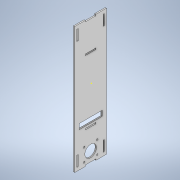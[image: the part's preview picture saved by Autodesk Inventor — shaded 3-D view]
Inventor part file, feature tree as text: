
AUTODESK INVENTOR PART (.ipt)
format: ipt  version: 2020 (Build 240168000, 168)  size: 261,120 bytes
history: native  units: in
note: dims shown in document units (in); Inventor stores cm internally (conversion verified against a paired STEP export)
features: sketch x12, extrude x11
ambient origin geometry x8: Origin, YZ Plane, XZ Plane, XY Plane, X Axis, Y Axis, Z Axis, Center Point
bodies: Solid1 (feature_tree)
feature tree (23):
  extrude  "Extrusion1"  Depth=0.1181in TaperAngle=0.0deg
  extrude  "Extrusion2"  Depth=0.1181in
  extrude  "Extrusion3"  Depth=0.1181in
  extrude  "Extrusion4"  Depth=0.1181in
  extrude  "Extrusion5"  Depth=0.1181in
  extrude  "Extrusion6"  Depth=0.1181in
  sketch  "Sketch7"  dims[d47=0.3937in d48=0.1181in]
  extrude  "Extrusion7"  Depth=0.1181in
  extrude  "Extrusion8"  Depth=0.3937in
  extrude  "Extrusion9"  Depth=1.1811in TaperAngle=0.0deg
  extrude  "Extrusion10"  Depth=0.5906in
  extrude  "Extrusion11"  Depth=0.3937in TaperAngle=0.0deg
  sketch  "Sketch1"  dims[d1=11.811in d9=0.1181in d10=0.0in]
  sketch  "Sketch2"  dims[d22=0.1181in d23=0.0in d29=0.1181in]
  sketch  "Sketch3"  dims[d30=0.1181in d31=0.1181in]
  sketch  "Sketch4"  dims[d32=0.1181in d33=0.9449in]
  sketch  "Sketch5"  dims[d34=0.1181in d35=0.0in d38=0.1181in]
  sketch  "Sketch6"  dims[d39=0.3937in d46=0.1181in]
  sketch  "Sketch8"  dims[d49=0.3937in d50=0.3937in]
  sketch  "Sketch9"  dims[d51=0.1181in d52=1.1811in d53=0.0in]
  sketch  "Sketch10"  dims[d59=0.3937in d60=0.0in d62=0.5906in]
  sketch  "Sketch11"  dims[d63=0.5906in d64=0.3937in d65=0.0in]
  sketch  "Sketch12"  dims[d66=0.1181in d67=0.0in d75=0.1575in d76=0.1575in d77=0.1575in d78=0.1575in d79=0.9449in d80=0.1181in d81=0.0in d82=1.0827in d83=0.3937in d84=0.0in d88=0.1181in d95=0.3937in d96=0.0in d97=0.1181in d98=0.0in d85=0.1969in d86=0.0344in]
